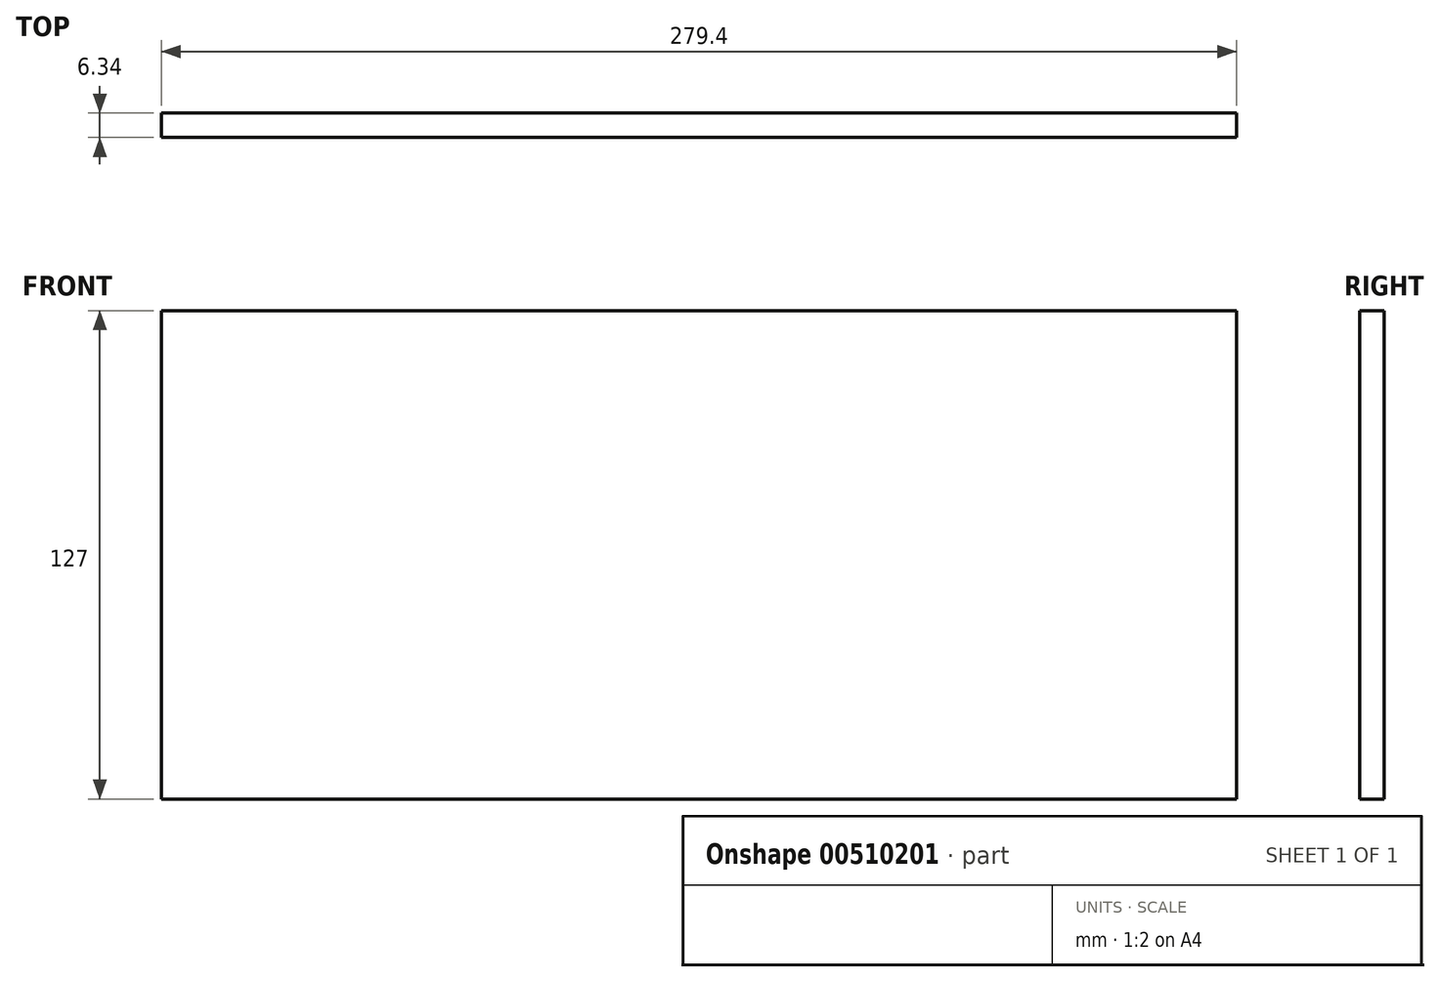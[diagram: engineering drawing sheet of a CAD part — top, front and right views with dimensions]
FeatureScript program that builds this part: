
annotation { "Feature Type Name" : "Feature", "Feature Type Description" : "" }
export const myFeature = defineFeature(function(context is Context, id is Id, definition is map)
    precondition{}
    {
        {
            var Q0;
            Q0=qCreatedBy(makeId("Front.planeOp"),FACE);
            var sketch = newSketch(context, id + "F0", { "sketchPlane" : qUnion([Q0])});
            skLineSegment(sketch, "E0.bottom", {"start": v(139.7, -63.5) * mm, "end": v(-139.7, -63.5) * mm});
            skLineSegment(sketch, "E0.top", {"start": v(139.7, 63.5) * mm, "end": v(-139.7, 63.5) * mm});
            skLineSegment(sketch, "E0.left", {"start": v(139.7, -63.5) * mm, "end": v(139.7, 63.5) * mm});
            skLineSegment(sketch, "E0.right", {"start": v(-139.7, -63.5) * mm, "end": v(-139.7, 63.5) * mm});
            skPoint(sketch, "E0.middle", {"position": v(0, 0) * mm});
            skSolve(sketch);
        }
        {
            var Q0;
            Q0=makeQuery(id+"F0.imprint","IMPRINT",FACE,{"disambiguationData":[TD([[makeQuery(id+"F0.imprint","IMPRINT",EDGE,{"derivedFrom":sQuery(id+"F0.wireOp",EDGE,"E0.bottom")}),-1.0]])]});
            extrude(context, id + "F1", {"entities" : qUnion([Q0]), "endBound" : BoundingType.SYMMETRIC, "depth" : 6.35 * mm});
        }
    });
